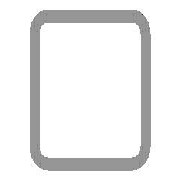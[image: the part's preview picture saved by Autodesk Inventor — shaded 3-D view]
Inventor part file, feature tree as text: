
AUTODESK INVENTOR PART (.ipt)
format: ipt  version: 2022 (Build 260153000, 153)  size: 179,200 bytes
history: native  units: mm (DEFAULTED — no unit token found)
features: other x5, sketch x2, sweep x1, plane x1
ambient origin geometry x8: Origin, YZ Plane, XZ Plane, XY Plane, X Axis, Y Axis, Z Axis, Center Point
bodies: Solid1 (feature_tree), Body (feature_tree)
feature tree (9):
  parser-record x1  (decoder bookkeeping rows leaked as tree rows — omitted from the tree; the rows remain in map.json)
  other  "Driven Length"
  other  "Start Plane"
  other  "End Plane"
  sweep  "Sweep Path"
  other  "Orientation Work Plane"
  sketch  "Sketch3"  dims[d7=7.5mm d10=40.0mm]
  plane  "Work Plane3"
  sketch  "Sketch4"  dims[d11=40.0mm d12=5.0mm d13=-0.0mm d14=2995.406592mm d15=20.0mm d16=20.0mm d17=90.0deg d18=2995.406592mm d19=0.0mm d20=0.0mm]
